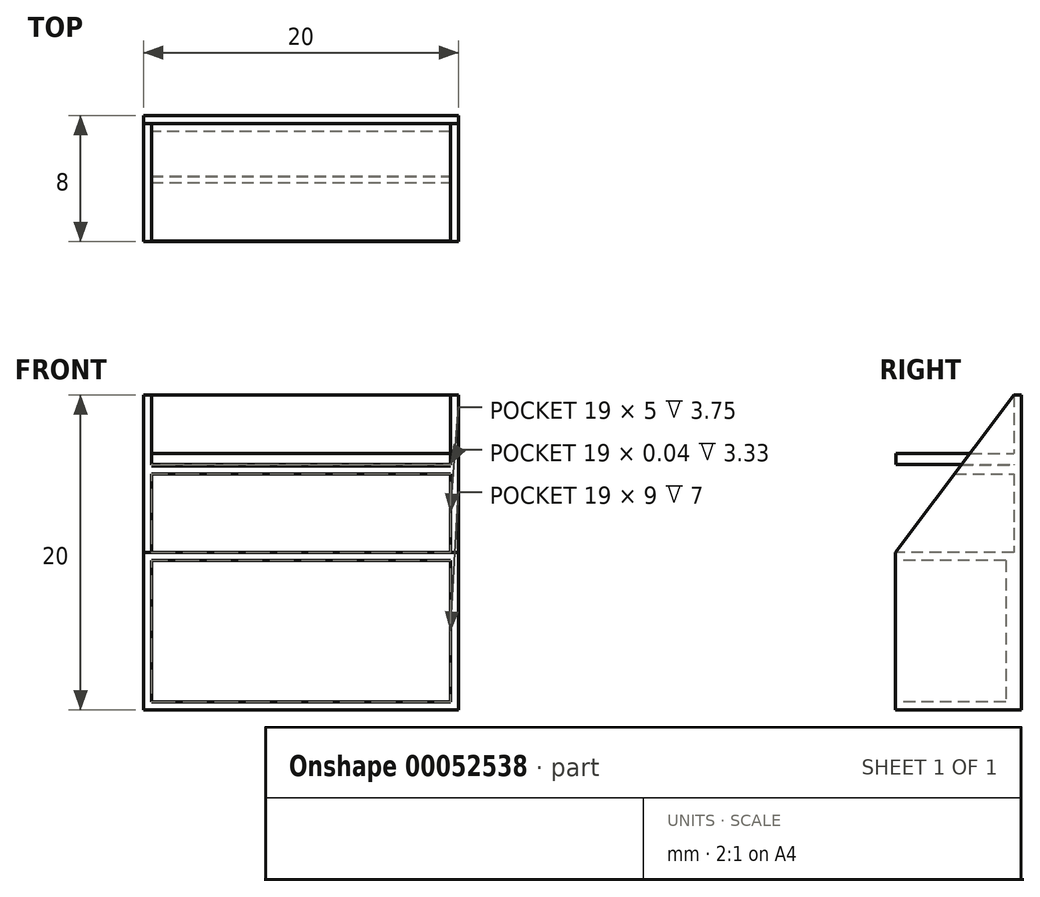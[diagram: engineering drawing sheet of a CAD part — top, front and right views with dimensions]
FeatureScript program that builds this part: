
annotation { "Feature Type Name" : "Feature", "Feature Type Description" : "" }
export const myFeature = defineFeature(function(context is Context, id is Id, definition is map)
    precondition{}
    {
        {
            var Q0;
            Q0=qCreatedBy(makeId("Top.planeOp"),FACE);
            var sketch = newSketch(context, id + "F0", { "sketchPlane" : qUnion([Q0])});
            skLineSegment(sketch, "E0.bottom", {"start": v(-1.7, 8) * mm, "end": v(18.3, 8) * mm});
            skLineSegment(sketch, "E0.top", {"start": v(-1.7, 0) * mm, "end": v(18.3, 0) * mm});
            skLineSegment(sketch, "E0.left", {"start": v(-1.7, 8) * mm, "end": v(-1.7, 0) * mm});
            skLineSegment(sketch, "E0.right", {"start": v(18.3, 8) * mm, "end": v(18.3, 0) * mm});
            skSolve(sketch);
        }
        {
            var Q0;
            Q0=makeQuery(id+"F0.imprint","IMPRINT",FACE,{"disambiguationData":[TD([[makeQuery(id+"F0.imprint","IMPRINT",EDGE,{"derivedFrom":sQuery(id+"F0.wireOp",EDGE,"E0.bottom")}),-1.0]])]});
            extrude(context, id + "F1", {"entities" : qUnion([Q0]), "depth" : 5 * mm});
        }
        {
            var Q0;
            Q0=makeQuery(id+"F1.opExtrude","CAP_FACE",FACE,{"disambiguationData":[OSD([sQuery(id+"F0.wireOp",EDGE,"E0.bottom"),sQuery(id+"F0.wireOp",EDGE,"E0.top"),sQuery(id+"F0.wireOp",EDGE,"E0.left"),sQuery(id+"F0.wireOp",EDGE,"E0.right")])],"isStart":false});
            var sketch = newSketch(context, id + "F2", { "sketchPlane" : qUnion([Q0])});
            skLineSegment(sketch, "E1.bottom", {"start": v(-1.7, 8) * mm, "end": v(18.3, 8) * mm});
            skLineSegment(sketch, "E1.top", {"start": v(-1.7, 7.5) * mm, "end": v(18.3, 7.5) * mm});
            skLineSegment(sketch, "E1.left", {"start": v(-1.7, 8) * mm, "end": v(-1.7, 7.5) * mm});
            skLineSegment(sketch, "E1.right", {"start": v(18.3, 8) * mm, "end": v(18.3, 7.5) * mm});
            skSolve(sketch);
        }
        {
            var Q0;
            Q0 = qSketchRegion(id + "F2", true);
            extrude(context, id + "F3", {"entities" : qUnion([Q0]), "operationType" : NewBodyOperationType.ADD, "depth" : 10 * mm});
        }
        {
            var Q0;
            Q0=makeQuery(id+"F3.boolean.opBoolean","MERGE",FACE,{"derivedFrom":[makeQuery(id+"F1.opExtrude","SWEPT_FACE",FACE,{"disambiguationData":[OSD([sQuery(id+"F0.wireOp",EDGE,"E0.left")])]}),makeQuery(id+"F3.opExtrude","SWEPT_FACE",FACE,{"disambiguationData":[OSD([sQuery(id+"F2.wireOp",EDGE,"E1.left")])]})]});
            var sketch = newSketch(context, id + "F4", { "sketchPlane" : qUnion([Q0])});
            skLineSegment(sketch, "E2", {"start": v(0, 5) * mm, "end": v(-7.5, 15) * mm});
            skSolve(sketch);
        }
        {
            var Q0;
            Q0=makeQuery(id+"F4.imprint","IMPRINT",FACE,{"disambiguationData":[TD([[makeQuery(id+"F4.imprint","IMPRINT",EDGE,{"derivedFrom":sQuery(id+"F4.wireOp",EDGE,"E2")}),1.0]])]});
            extrude(context, id + "F5", {"entities" : qUnion([Q0]), "oppositeDirection" : true, "depth" : 0.5 * mm});
        }
        {
            var Q0;
            Q0=makeQuery(id+"F3.boolean.opBoolean","MERGE",FACE,{"derivedFrom":[makeQuery(id+"F1.opExtrude","SWEPT_FACE",FACE,{"disambiguationData":[OSD([sQuery(id+"F0.wireOp",EDGE,"E0.right")])]}),makeQuery(id+"F3.opExtrude","SWEPT_FACE",FACE,{"disambiguationData":[OSD([sQuery(id+"F2.wireOp",EDGE,"E1.right")])]})]});
            var sketch = newSketch(context, id + "F6", { "sketchPlane" : qUnion([Q0])});
            skLineSegment(sketch, "E3", {"start": v(7.5, 15) * mm, "end": v(0, 5) * mm});
            skSolve(sketch);
        }
        {
            var Q0;
            Q0=makeQuery(id+"F6.imprint","IMPRINT",FACE,{"disambiguationData":[TD([[makeQuery(id+"F6.imprint","IMPRINT",EDGE,{"derivedFrom":sQuery(id+"F6.wireOp",EDGE,"E3")}),1.0]])]});
            extrude(context, id + "F7", {"entities" : qUnion([Q0]), "oppositeDirection" : true, "depth" : 0.5 * mm});
        }
        {
            var Q0;
            Q0=makeQuery(id+"F1.opExtrude","CAP_FACE",FACE,{"disambiguationData":[OSD([sQuery(id+"F0.wireOp",EDGE,"E0.bottom"),sQuery(id+"F0.wireOp",EDGE,"E0.top"),sQuery(id+"F0.wireOp",EDGE,"E0.left"),sQuery(id+"F0.wireOp",EDGE,"E0.right")])],"isStart":true});
            extrude(context, id + "F8", {"entities" : qUnion([Q0]), "operationType" : NewBodyOperationType.ADD, "depth" : 5 * mm});
        }
        {
            var Q0;
            Q0=makeQuery(id+"F3.opExtrude","SWEPT_FACE",FACE,{"disambiguationData":[OSD([sQuery(id+"F2.wireOp",EDGE,"E1.top")])]});
            var sketch = newSketch(context, id + "F9", { "sketchPlane" : qUnion([Q0])});
            skLineSegment(sketch, "E4", {"start": v(-1.2, 11.3) * mm, "end": v(17.8, 11.3) * mm});
            skLineSegment(sketch, "E5", {"start": v(17.8, 11.3) * mm, "end": v(17.8, 10.6) * mm});
            skLineSegment(sketch, "E6", {"start": v(17.8, 10.6) * mm, "end": v(-1.2, 10.6) * mm});
            skLineSegment(sketch, "E7", {"start": v(-1.2, 10.6) * mm, "end": v(-1.2, 11.3) * mm});
            skSolve(sketch);
        }
        {
            var Q0;
            Q0 = qSketchRegion(id + "F9", true);
            extrude(context, id + "F10", {"entities" : qUnion([Q0]), "operationType" : NewBodyOperationType.ADD, "depth" : 7.47 * mm});
        }
        {
            var Q0;
            Q0=makeQuery(id+"F3.opExtrude","SWEPT_FACE",FACE,{"disambiguationData":[OSD([sQuery(id+"F2.wireOp",EDGE,"E1.top")])]});
            var sketch = newSketch(context, id + "F11", { "sketchPlane" : qUnion([Q0])});
            skLineSegment(sketch, "E8.bottom", {"start": v(-1.2, 10.56) * mm, "end": v(17.8, 10.56) * mm});
            skLineSegment(sketch, "E8.top", {"start": v(-1.2, 10) * mm, "end": v(17.8, 10) * mm});
            skLineSegment(sketch, "E8.left", {"start": v(-1.2, 10.56) * mm, "end": v(-1.2, 10) * mm});
            skLineSegment(sketch, "E8.right", {"start": v(17.8, 10.56) * mm, "end": v(17.8, 10) * mm});
            skSolve(sketch);
        }
        {
            var Q0;
            Q0=makeQuery(id+"F11.imprint","IMPRINT",FACE,{"disambiguationData":[TD([[makeQuery(id+"F11.imprint","IMPRINT",EDGE,{"derivedFrom":sQuery(id+"F11.wireOp",EDGE,"E8.bottom")}),-1.0]])]});
            extrude(context, id + "F12", {"entities" : qUnion([Q0]), "operationType" : NewBodyOperationType.ADD, "depth" : 4 * mm});
        }
        {
            var Q0;
            Q0=makeQuery(id+"F12.opExtrude","SWEPT_FACE",FACE,{"disambiguationData":[OSD([sQuery(id+"F11.wireOp",EDGE,"E8.right")])]});
            var sketch = newSketch(context, id + "F13", { "sketchPlane" : qUnion([Q0])});
            skLineSegment(sketch, "E9", {"start": v(4.12, 10.5) * mm, "end": v(3.75, 10) * mm});
            skLineSegment(sketch, "E10", {"start": v(3.75, 10) * mm, "end": v(3.5, 10) * mm});
            skLineSegment(sketch, "E11", {"start": v(3.5, 10) * mm, "end": v(3.5, 10.56) * mm});
            skLineSegment(sketch, "E12", {"start": v(3.5, 10.56) * mm, "end": v(4.17, 10.56) * mm});
            skLineSegment(sketch, "E13", {"start": v(4.17, 10.56) * mm, "end": v(4.12, 10.5) * mm});
            skSolve(sketch);
        }
        {
            var Q0;
            Q0=makeQuery(id+"F13.imprint","IMPRINT",FACE,{"disambiguationData":[TD([[makeQuery(id+"F13.imprint","IMPRINT",EDGE,{"derivedFrom":sQuery(id+"F13.wireOp",EDGE,"E9")}),-1.0]])]});
            extrude(context, id + "F14", {"entities" : qUnion([Q0]), "operationType" : NewBodyOperationType.REMOVE, "oppositeDirection" : true, "depth" : 25 * mm});
        }
        {
            var Q0;
            {var subQ0=sQuery(id+"F0.wireOp",EDGE,"E0.top");Q0=makeQuery(id+"F8.boolean.opBoolean","MERGE",FACE,{"derivedFrom":[makeQuery(id+"F1.opExtrude","SWEPT_FACE",FACE,{"disambiguationData":[OSD([subQ0])]}),makeQuery(id+"F8.opExtrude","SWEPT_FACE",FACE,{"disambiguationData":[OSD([subQ0])]})]});}
            var sketch = newSketch(context, id + "F15", { "sketchPlane" : qUnion([Q0])});
            skLineSegment(sketch, "E14", {"start": v(-1.2, 5) * mm, "end": v(-1.2, 4.5) * mm});
            skLineSegment(sketch, "E15", {"start": v(-1.2, 4.5) * mm, "end": v(-1.7, 4.5) * mm});
            skLineSegment(sketch, "E16", {"start": v(-1.2, -5) * mm, "end": v(-1.2, -4.5) * mm});
            skLineSegment(sketch, "E17", {"start": v(-1.2, -4.5) * mm, "end": v(-1.7, -4.5) * mm});
            skLineSegment(sketch, "E18", {"start": v(17.8, 5) * mm, "end": v(17.8, 4.5) * mm});
            skLineSegment(sketch, "E19", {"start": v(18.47, -4.46) * mm, "end": v(17.8, -4.5) * mm});
            skLineSegment(sketch, "E20", {"start": v(18.3, -4.48) * mm, "end": v(17.8, -4.5) * mm});
            skLineSegment(sketch, "E21", {"start": v(17.8, -4.5) * mm, "end": v(17.8, -5) * mm});
            skLineSegment(sketch, "E22", {"start": v(17.8, 4.5) * mm, "end": v(18.3, 4.5) * mm});
            skLineSegment(sketch, "E23.bottom", {"start": v(17.8, 4.5) * mm, "end": v(-1.2, 4.5) * mm});
            skLineSegment(sketch, "E23.top", {"start": v(17.8, -4.5) * mm, "end": v(-1.2, -4.5) * mm});
            skLineSegment(sketch, "E23.left", {"start": v(17.8, 4.5) * mm, "end": v(17.8, -4.5) * mm});
            skLineSegment(sketch, "E23.right", {"start": v(-1.2, 4.5) * mm, "end": v(-1.2, -4.5) * mm});
            skSolve(sketch);
        }
        {
            var Q0;
            Q0=makeQuery(id+"F15.imprint","IMPRINT",FACE,{"disambiguationData":[TD([[makeQuery(id+"F15.imprint","IMPRINT",EDGE,{"derivedFrom":sQuery(id+"F15.wireOp",EDGE,"E23.bottom")}),1.0]])]});
            extrude(context, id + "F16", {"entities" : qUnion([Q0]), "operationType" : NewBodyOperationType.REMOVE, "oppositeDirection" : true, "depth" : 7 * mm});
        }
    });
